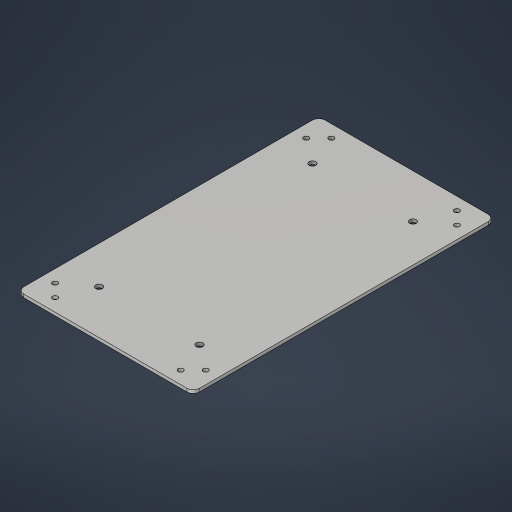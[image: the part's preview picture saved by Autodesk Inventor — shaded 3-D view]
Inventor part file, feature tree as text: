
AUTODESK INVENTOR PART (.ipt)
format: ipt  version: 2023 (Build 270158000, 158)  size: 221,696 bytes
history: native  units: in
note: dims shown in document units (in); Inventor stores cm internally (conversion verified against a paired STEP export)
features: sketch x2, other x2, sheet_metal_op x1, chamfer x1
ambient origin geometry x8: Origin, YZ Plane, XZ Plane, XY Plane, X Axis, Y Axis, Z Axis, Center Point
bodies: Solid1 (feature_tree)
feature tree (6):
  sheet_metal_op  "Face1"
  chamfer  "Corner Round1"
  sketch  "Sketch1"  dims[d0=7.0in]
  other  "Plate1"
  sketch  "Sketch2"  dims[d1=12.0in d2=0.125in d3=0.25in d4=0.2031in d5=0.5in d6=1.0in d7=0.5in d8=1.0in d9=0.125in d10=0.0in d11=4.0in d12=0.26in d13=8.5in]
  other  "Cut1"
